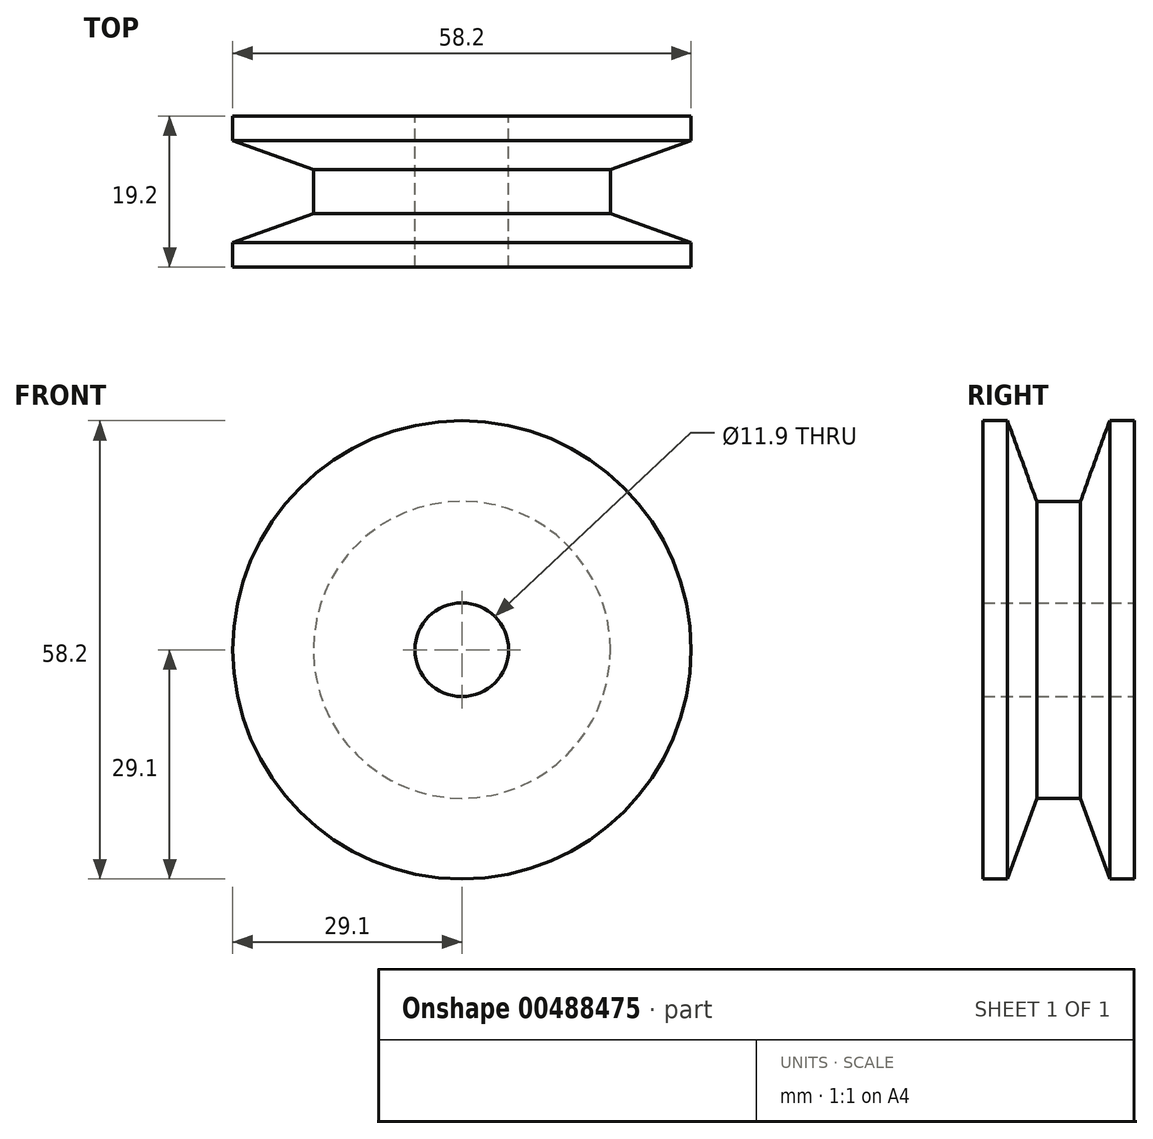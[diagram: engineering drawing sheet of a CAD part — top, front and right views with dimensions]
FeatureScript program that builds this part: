
annotation { "Feature Type Name" : "Feature", "Feature Type Description" : "" }
export const myFeature = defineFeature(function(context is Context, id is Id, definition is map)
    precondition{}
    {
        {
            var Q0;
            Q0=qCreatedBy(makeId("Right.planeOp"),FACE);
            var sketch = newSketch(context, id + "F0", { "sketchPlane" : qUnion([Q0])});
            skLineSegment(sketch, "E0", {"start": v(0, 5.95) * mm, "end": v(-19.2, 5.95) * mm});
            skLineSegment(sketch, "E1", {"start": v(-19.2, 5.95) * mm, "end": v(-19.2, 29.1) * mm});
            skLineSegment(sketch, "E2", {"start": v(-19.2, 29.1) * mm, "end": v(-16.1, 29.1) * mm});
            skLineSegment(sketch, "E3", {"start": v(-16.1, 29.1) * mm, "end": v(-12.38, 18.87) * mm});
            skLineSegment(sketch, "E4", {"start": v(-12.38, 18.87) * mm, "end": v(-6.83, 18.87) * mm});
            skLineSegment(sketch, "E5", {"start": v(-6.83, 18.87) * mm, "end": v(-3.1, 29.1) * mm});
            skLineSegment(sketch, "E6", {"start": v(-3.1, 29.1) * mm, "end": v(0, 29.1) * mm});
            skLineSegment(sketch, "E7", {"start": v(0, 29.1) * mm, "end": v(0, 5.95) * mm});
            skLineSegment(sketch, "E8", {"start": v(0, 0) * mm, "end": v(-28.77, 0) * mm, "construction": true});
            skSolve(sketch);
        }
        {
            var Q0;
            Q0=makeQuery(id+"F0.imprint","IMPRINT",FACE,{"disambiguationData":[TD([[makeQuery(id+"F0.imprint","IMPRINT",EDGE,{"derivedFrom":sQuery(id+"F0.wireOp",EDGE,"E0")}),-1.0]])]});
            var Q1;
            Q1=sQuery(id+"F0.wireOp",EDGE,"E8");
            revolve(context, id + "F1", {"entities" : qUnion([Q0]), "axis" : qUnion([Q1]), "revolveType" : RevolveType.FULL});
        }
    });
